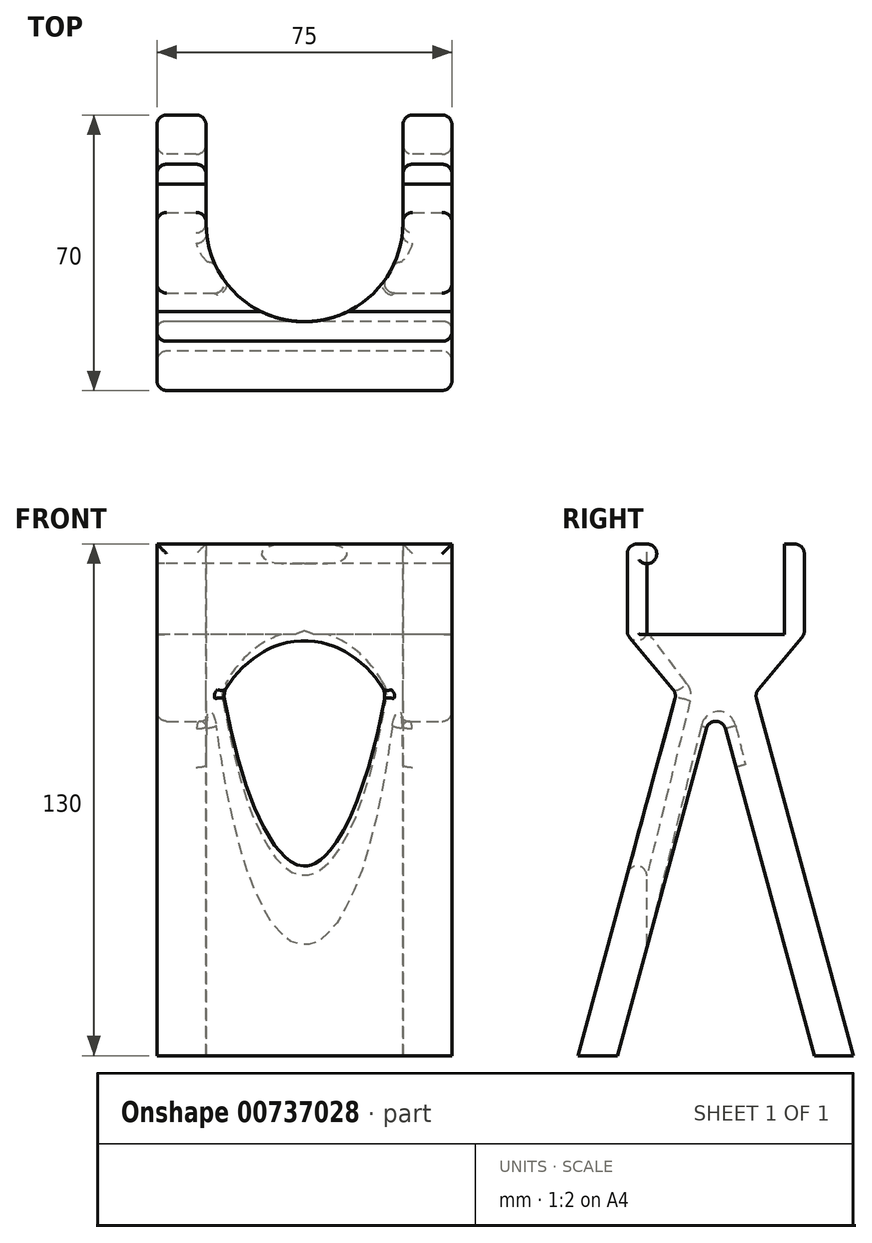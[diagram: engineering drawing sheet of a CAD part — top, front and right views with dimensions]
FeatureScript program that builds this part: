
annotation { "Feature Type Name" : "Feature", "Feature Type Description" : "" }
export const myFeature = defineFeature(function(context is Context, id is Id, definition is map)
    precondition{}
    {
        {
            var Q0;
            Q0=qCreatedBy(makeId("Right.planeOp"),FACE);
            var sketch = newSketch(context, id + "F0", { "sketchPlane" : qUnion([Q0])});
            skLineSegment(sketch, "E0", {"start": v(-104.17, 14.75) * mm, "end": v(-104.17, -8.25) * mm});
            skLineSegment(sketch, "E1", {"start": v(-104.17, -8.25) * mm, "end": v(-91.67, -23.25) * mm});
            skLineSegment(sketch, "E2", {"start": v(-91.67, -23.25) * mm, "end": v(-116.67, -115.25) * mm});
            skLineSegment(sketch, "E3", {"start": v(-116.67, -115.25) * mm, "end": v(-106.67, -115.25) * mm});
            skLineSegment(sketch, "E4", {"start": v(-106.67, -115.25) * mm, "end": v(-81.67, -23.25) * mm});
            skLineSegment(sketch, "E5", {"start": v(-81.67, -23.25) * mm, "end": v(-56.67, -115.25) * mm});
            skLineSegment(sketch, "E6", {"start": v(-56.67, -115.25) * mm, "end": v(-46.67, -115.25) * mm});
            skLineSegment(sketch, "E7", {"start": v(-46.67, -115.25) * mm, "end": v(-71.67, -23.25) * mm});
            skLineSegment(sketch, "E8", {"start": v(-71.67, -23.25) * mm, "end": v(-59.17, -8.25) * mm});
            skLineSegment(sketch, "E9", {"start": v(-59.17, -8.25) * mm, "end": v(-59.17, 14.75) * mm});
            skLineSegment(sketch, "E10", {"start": v(-59.17, 14.75) * mm, "end": v(-64.17, 14.75) * mm});
            skLineSegment(sketch, "E11", {"start": v(-64.17, 14.75) * mm, "end": v(-64.17, -8.25) * mm});
            skLineSegment(sketch, "E12", {"start": v(-64.17, -8.25) * mm, "end": v(-99.17, -8.25) * mm});
            skLineSegment(sketch, "E13", {"start": v(-99.17, -8.25) * mm, "end": v(-99.17, 9.75) * mm});
            skLineSegment(sketch, "E14", {"start": v(-99.17, 14.75) * mm, "end": v(-104.17, 14.75) * mm});
            skLineSegment(sketch, "E15", {"start": v(-81.67, -8.25) * mm, "end": v(-81.67, -125.81) * mm, "construction": true});
            skLineSegment(sketch, "E16", {"start": v(-81.67, -8.25) * mm, "end": v(-81.67, 62.4) * mm, "construction": true});
            skArc(sketch, "E17", {"start": v(-99.17, 9.75) * mm, "mid": v(-96.67, 12.25) * mm, "end": v(-99.17, 14.75) * mm});
            skSolve(sketch);
        }
        {
            var Q0;
            Q0 = qSketchRegion(id + "F0", true);
            extrude(context, id + "F1", {"entities" : qUnion([Q0]), "depth" : 75 * mm, "offsetDistance" : 25 * mm});
        }
        {
            var Q0;
            Q0=makeQuery(id+"F1.opExtrude","SWEPT_FACE",FACE,{"disambiguationData":[OSD([sQuery(id+"F0.wireOp",EDGE,"E10")])]});
            var sketch = newSketch(context, id + "F2", { "sketchPlane" : qUnion([Q0])});
            skLineSegment(sketch, "E18.bottom", {"start": v(12.5, -31.92) * mm, "end": v(62.5, -31.92) * mm});
            skLineSegment(sketch, "E18.left", {"start": v(12.5, -31.92) * mm, "end": v(12.5, -74.17) * mm});
            skLineSegment(sketch, "E18.right", {"start": v(62.5, -31.92) * mm, "end": v(62.5, -74.17) * mm});
            skArc(sketch, "E19", {"start": v(12.5, -74.17) * mm, "mid": v(37.5, -99.17) * mm, "end": v(62.5, -74.17) * mm});
            skLineSegment(sketch, "E20", {"start": v(37.5, -24.96) * mm, "end": v(37.5, -154.67) * mm, "construction": true});
            skLineSegment(sketch, "E21", {"start": v(0, -81.67) * mm, "end": v(75, -81.67) * mm, "construction": true});
            skPoint(sketch, "E22", {"position": v(37.5, -31.92) * mm});
            skPoint(sketch, "E23", {"position": v(37.5, -81.67) * mm});
            skSolve(sketch);
        }
        {
            var Q0;
            Q0 = qSketchRegion(id + "F2", true);
            var Q1;
            Q1=makeQuery(id+"F1.opExtrude","SWEPT_FACE",FACE,{"disambiguationData":[OSD([sQuery(id+"F0.wireOp",EDGE,"E6")])]});
            var Q2;
            Q2=makeQuery(id+"F1.opExtrude","SWEPT_FACE",FACE,{"disambiguationData":[OSD([sQuery(id+"F0.wireOp",EDGE,"E6")])]});
            extrude(context, id + "F3", {"entities" : qUnion([Q0]), "operationType" : NewBodyOperationType.REMOVE, "endBound" : BoundingType.UP_TO_SURFACE, "oppositeDirection" : true, "depth" : 0 * mm, "endBoundEntityFace" : qUnion([Q1]), "offsetDistance" : 25 * mm});
        }
        {
            var Q0;
            Q0=makeQuery(id+"F1.opExtrude","CAP_EDGE",EDGE,{"disambiguationData":[OSD([sQuery(id+"F0.wireOp",EDGE,"E7")])],"isStart":true});
            var Q1;
            Q1=makeQuery(id+"F1.opExtrude","CAP_EDGE",EDGE,{"disambiguationData":[OSD([sQuery(id+"F0.wireOp",EDGE,"E8")])],"isStart":true});
            var Q2;
            Q2=makeQuery(id+"F1.opExtrude","CAP_EDGE",EDGE,{"disambiguationData":[OSD([sQuery(id+"F0.wireOp",EDGE,"E9")])],"isStart":true});
            var Q3;
            {var subQ0=sQuery(id+"F0.wireOp",EDGE,"E10");var subQ1=sQuery(id+"F0.wireOp",EDGE,"E9");Q3=makeQuery(id+"F3.boolean.opBoolean","SPLIT",EDGE,{"disambiguationData":[TD([makeQuery(id+"F3.opExtrude","SWEPT_FACE",FACE,{"disambiguationData":[OSD([sQuery(id+"F2.wireOp",EDGE,"E18.left")])]})])],"derivedFrom":makeQuery(id+"F1.opExtrude","SWEPT_EDGE",EDGE,{"disambiguationData":[OSD([subQ1,subQ0])]})});}
            var Q4;
            Q4=makeQuery(id+"F3.boolean.opBoolean","INTERSECT",EDGE,{"derivedFrom":[makeQuery(id+"F1.opExtrude","SWEPT_FACE",FACE,{"disambiguationData":[OSD([sQuery(id+"F0.wireOp",EDGE,"E9")])]}),makeQuery(id+"F3.opExtrude","SWEPT_FACE",FACE,{"disambiguationData":[OSD([sQuery(id+"F2.wireOp",EDGE,"E18.left")])]})]});
            var Q5;
            Q5=makeQuery(id+"F3.boolean.opBoolean","INTERSECT",EDGE,{"derivedFrom":[makeQuery(id+"F1.opExtrude","SWEPT_FACE",FACE,{"disambiguationData":[OSD([sQuery(id+"F0.wireOp",EDGE,"E8")])]}),makeQuery(id+"F3.opExtrude","SWEPT_FACE",FACE,{"disambiguationData":[OSD([sQuery(id+"F2.wireOp",EDGE,"E18.left")])]})]});
            var Q6;
            Q6=makeQuery(id+"F3.boolean.opBoolean","INTERSECT",EDGE,{"derivedFrom":[makeQuery(id+"F1.opExtrude","SWEPT_FACE",FACE,{"disambiguationData":[OSD([sQuery(id+"F0.wireOp",EDGE,"E7")])]}),makeQuery(id+"F3.opExtrude","SWEPT_FACE",FACE,{"disambiguationData":[OSD([sQuery(id+"F2.wireOp",EDGE,"E18.left")])]})]});
            var Q7;
            {var subQ0=sQuery(id+"F0.wireOp",EDGE,"E8");var subQ1=sQuery(id+"F0.wireOp",EDGE,"E7");Q7=makeQuery(id+"F3.boolean.opBoolean","SPLIT",EDGE,{"disambiguationData":[TD([makeQuery(id+"F3.opExtrude","SWEPT_FACE",FACE,{"disambiguationData":[OSD([sQuery(id+"F2.wireOp",EDGE,"E18.left")])]})])],"derivedFrom":makeQuery(id+"F1.opExtrude","SWEPT_EDGE",EDGE,{"disambiguationData":[OSD([subQ1,subQ0])]})});}
            var Q8;
            {var subQ0=sQuery(id+"F0.wireOp",EDGE,"E9");var subQ1=sQuery(id+"F0.wireOp",EDGE,"E8");Q8=makeQuery(id+"F3.boolean.opBoolean","SPLIT",EDGE,{"disambiguationData":[TD([makeQuery(id+"F3.opExtrude","SWEPT_FACE",FACE,{"disambiguationData":[OSD([sQuery(id+"F2.wireOp",EDGE,"E18.left")])]})])],"derivedFrom":makeQuery(id+"F1.opExtrude","SWEPT_EDGE",EDGE,{"disambiguationData":[OSD([subQ1,subQ0])]})});}
            var Q9;
            Q9=makeQuery(id+"F3.boolean.opBoolean","INTERSECT",EDGE,{"derivedFrom":[makeQuery(id+"F1.opExtrude","SWEPT_FACE",FACE,{"disambiguationData":[OSD([sQuery(id+"F0.wireOp",EDGE,"E7")])]}),makeQuery(id+"F3.opExtrude","SWEPT_FACE",FACE,{"disambiguationData":[OSD([sQuery(id+"F2.wireOp",EDGE,"E18.right")])]})]});
            var Q10;
            Q10=makeQuery(id+"F3.boolean.opBoolean","INTERSECT",EDGE,{"derivedFrom":[makeQuery(id+"F1.opExtrude","SWEPT_FACE",FACE,{"disambiguationData":[OSD([sQuery(id+"F0.wireOp",EDGE,"E8")])]}),makeQuery(id+"F3.opExtrude","SWEPT_FACE",FACE,{"disambiguationData":[OSD([sQuery(id+"F2.wireOp",EDGE,"E18.right")])]})]});
            var Q11;
            Q11=makeQuery(id+"F3.boolean.opBoolean","INTERSECT",EDGE,{"derivedFrom":[makeQuery(id+"F1.opExtrude","SWEPT_FACE",FACE,{"disambiguationData":[OSD([sQuery(id+"F0.wireOp",EDGE,"E9")])]}),makeQuery(id+"F3.opExtrude","SWEPT_FACE",FACE,{"disambiguationData":[OSD([sQuery(id+"F2.wireOp",EDGE,"E18.right")])]})]});
            var Q12;
            {var subQ0=sQuery(id+"F0.wireOp",EDGE,"E10");var subQ1=sQuery(id+"F0.wireOp",EDGE,"E9");Q12=makeQuery(id+"F3.boolean.opBoolean","SPLIT",EDGE,{"disambiguationData":[TD([makeQuery(id+"F3.opExtrude","SWEPT_FACE",FACE,{"disambiguationData":[OSD([sQuery(id+"F2.wireOp",EDGE,"E18.right")])]})])],"derivedFrom":makeQuery(id+"F1.opExtrude","SWEPT_EDGE",EDGE,{"disambiguationData":[OSD([subQ1,subQ0])]})});}
            var Q13;
            Q13=makeQuery(id+"F1.opExtrude","CAP_EDGE",EDGE,{"disambiguationData":[OSD([sQuery(id+"F0.wireOp",EDGE,"E9")])],"isStart":false});
            var Q14;
            Q14=makeQuery(id+"F1.opExtrude","CAP_EDGE",EDGE,{"disambiguationData":[OSD([sQuery(id+"F0.wireOp",EDGE,"E8")])],"isStart":false});
            var Q15;
            Q15=makeQuery(id+"F1.opExtrude","CAP_EDGE",EDGE,{"disambiguationData":[OSD([sQuery(id+"F0.wireOp",EDGE,"E7")])],"isStart":false});
            var Q16;
            {var subQ0=sQuery(id+"F0.wireOp",EDGE,"E8");var subQ1=sQuery(id+"F0.wireOp",EDGE,"E7");Q16=makeQuery(id+"F3.boolean.opBoolean","SPLIT",EDGE,{"disambiguationData":[TD([makeQuery(id+"F3.opExtrude","SWEPT_FACE",FACE,{"disambiguationData":[OSD([sQuery(id+"F2.wireOp",EDGE,"E18.right")])]})])],"derivedFrom":makeQuery(id+"F1.opExtrude","SWEPT_EDGE",EDGE,{"disambiguationData":[OSD([subQ1,subQ0])]})});}
            var Q17;
            {var subQ0=sQuery(id+"F0.wireOp",EDGE,"E9");var subQ1=sQuery(id+"F0.wireOp",EDGE,"E8");Q17=makeQuery(id+"F3.boolean.opBoolean","SPLIT",EDGE,{"disambiguationData":[TD([makeQuery(id+"F3.opExtrude","SWEPT_FACE",FACE,{"disambiguationData":[OSD([sQuery(id+"F2.wireOp",EDGE,"E18.right")])]})])],"derivedFrom":makeQuery(id+"F1.opExtrude","SWEPT_EDGE",EDGE,{"disambiguationData":[OSD([subQ1,subQ0])]})});}
            var Q18;
            Q18=makeQuery(id+"F1.opExtrude","CAP_EDGE",EDGE,{"disambiguationData":[OSD([sQuery(id+"F0.wireOp",EDGE,"E5")])],"isStart":false});
            var Q19;
            Q19=makeQuery(id+"F3.boolean.opBoolean","INTERSECT",EDGE,{"derivedFrom":[makeQuery(id+"F1.opExtrude","SWEPT_FACE",FACE,{"disambiguationData":[OSD([sQuery(id+"F0.wireOp",EDGE,"E5")])]}),makeQuery(id+"F3.opExtrude","SWEPT_FACE",FACE,{"disambiguationData":[OSD([sQuery(id+"F2.wireOp",EDGE,"E18.right")])]})]});
            var Q20;
            Q20=makeQuery(id+"F1.opExtrude","CAP_EDGE",EDGE,{"disambiguationData":[OSD([sQuery(id+"F0.wireOp",EDGE,"E4")])],"isStart":false});
            var Q21;
            Q21=makeQuery(id+"F1.opExtrude","CAP_EDGE",EDGE,{"disambiguationData":[OSD([sQuery(id+"F0.wireOp",EDGE,"E4")])],"isStart":true});
            var Q22;
            Q22=makeQuery(id+"F3.boolean.opBoolean","INTERSECT",EDGE,{"derivedFrom":[makeQuery(id+"F1.opExtrude","SWEPT_FACE",FACE,{"disambiguationData":[OSD([sQuery(id+"F0.wireOp",EDGE,"E4")])]}),makeQuery(id+"F3.opExtrude","SWEPT_FACE",FACE,{"disambiguationData":[OSD([sQuery(id+"F2.wireOp",EDGE,"E19")])]})]});
            var Q23;
            Q23=makeQuery(id+"F3.boolean.opBoolean","INTERSECT",EDGE,{"derivedFrom":[makeQuery(id+"F1.opExtrude","SWEPT_FACE",FACE,{"disambiguationData":[OSD([sQuery(id+"F0.wireOp",EDGE,"E2")])]}),makeQuery(id+"F3.opExtrude","SWEPT_FACE",FACE,{"disambiguationData":[OSD([sQuery(id+"F2.wireOp",EDGE,"E19")])]})]});
            var Q24;
            Q24=makeQuery(id+"F3.boolean.opBoolean","INTERSECT",EDGE,{"derivedFrom":[makeQuery(id+"F1.opExtrude","SWEPT_FACE",FACE,{"disambiguationData":[OSD([sQuery(id+"F0.wireOp",EDGE,"E1")])]}),makeQuery(id+"F3.opExtrude","SWEPT_FACE",FACE,{"disambiguationData":[OSD([sQuery(id+"F2.wireOp",EDGE,"E19")])]})]});
            var Q25;
            Q25=makeQuery(id+"F1.opExtrude","CAP_EDGE",EDGE,{"disambiguationData":[OSD([sQuery(id+"F0.wireOp",EDGE,"E2")])],"isStart":false});
            var Q26;
            Q26=makeQuery(id+"F1.opExtrude","CAP_EDGE",EDGE,{"disambiguationData":[OSD([sQuery(id+"F0.wireOp",EDGE,"E2")])],"isStart":true});
            var Q27;
            Q27=makeQuery(id+"F1.opExtrude","CAP_EDGE",EDGE,{"disambiguationData":[OSD([sQuery(id+"F0.wireOp",EDGE,"E5")])],"isStart":true});
            var Q28;
            Q28=makeQuery(id+"F3.boolean.opBoolean","INTERSECT",EDGE,{"derivedFrom":[makeQuery(id+"F1.opExtrude","SWEPT_FACE",FACE,{"disambiguationData":[OSD([sQuery(id+"F0.wireOp",EDGE,"E5")])]}),makeQuery(id+"F3.opExtrude","SWEPT_FACE",FACE,{"disambiguationData":[OSD([sQuery(id+"F2.wireOp",EDGE,"E18.left")])]})]});
            var Q29;
            Q29=makeQuery(id+"F1.opExtrude","SWEPT_EDGE",EDGE,{"disambiguationData":[OSD([sQuery(id+"F0.wireOp",EDGE,"E0"),sQuery(id+"F0.wireOp",EDGE,"E14")])]});
            var Q30;
            Q30=makeQuery(id+"F1.opExtrude","CAP_EDGE",EDGE,{"disambiguationData":[OSD([sQuery(id+"F0.wireOp",EDGE,"E1")])],"isStart":true});
            var Q31;
            Q31=makeQuery(id+"F1.opExtrude","CAP_EDGE",EDGE,{"disambiguationData":[OSD([sQuery(id+"F0.wireOp",EDGE,"E0")])],"isStart":true});
            var Q32;
            Q32=makeQuery(id+"F1.opExtrude","CAP_EDGE",EDGE,{"disambiguationData":[OSD([sQuery(id+"F0.wireOp",EDGE,"E1")])],"isStart":false});
            var Q33;
            Q33=makeQuery(id+"F1.opExtrude","CAP_EDGE",EDGE,{"disambiguationData":[OSD([sQuery(id+"F0.wireOp",EDGE,"E0")])],"isStart":false});
            var Q34;
            {var subQ0=sQuery(id+"F0.wireOp",EDGE,"E2");var subQ1=sQuery(id+"F0.wireOp",EDGE,"E1");Q34=makeQuery(id+"F3.boolean.opBoolean","SPLIT",EDGE,{"disambiguationData":[TD([makeQuery(id+"F1.opExtrude","CAP_FACE",FACE,{"disambiguationData":[OSD([sQuery(id+"F0.wireOp",EDGE,"E0"),subQ1,subQ0,sQuery(id+"F0.wireOp",EDGE,"E3"),sQuery(id+"F0.wireOp",EDGE,"E4"),sQuery(id+"F0.wireOp",EDGE,"E5"),sQuery(id+"F0.wireOp",EDGE,"E6"),sQuery(id+"F0.wireOp",EDGE,"E7"),sQuery(id+"F0.wireOp",EDGE,"E8"),sQuery(id+"F0.wireOp",EDGE,"E9"),sQuery(id+"F0.wireOp",EDGE,"E10"),sQuery(id+"F0.wireOp",EDGE,"E11"),sQuery(id+"F0.wireOp",EDGE,"E12"),sQuery(id+"F0.wireOp",EDGE,"E13"),sQuery(id+"F0.wireOp",EDGE,"E14"),sQuery(id+"F0.wireOp",EDGE,"E17")])],"isStart":true})])],"derivedFrom":makeQuery(id+"F1.opExtrude","SWEPT_EDGE",EDGE,{"disambiguationData":[OSD([subQ1,subQ0])]})});}
            var Q35;
            {var subQ0=sQuery(id+"F0.wireOp",EDGE,"E2");var subQ1=sQuery(id+"F0.wireOp",EDGE,"E1");Q35=makeQuery(id+"F3.boolean.opBoolean","SPLIT",EDGE,{"disambiguationData":[TD([makeQuery(id+"F1.opExtrude","CAP_FACE",FACE,{"disambiguationData":[OSD([sQuery(id+"F0.wireOp",EDGE,"E0"),subQ1,subQ0,sQuery(id+"F0.wireOp",EDGE,"E3"),sQuery(id+"F0.wireOp",EDGE,"E4"),sQuery(id+"F0.wireOp",EDGE,"E5"),sQuery(id+"F0.wireOp",EDGE,"E6"),sQuery(id+"F0.wireOp",EDGE,"E7"),sQuery(id+"F0.wireOp",EDGE,"E8"),sQuery(id+"F0.wireOp",EDGE,"E9"),sQuery(id+"F0.wireOp",EDGE,"E10"),sQuery(id+"F0.wireOp",EDGE,"E11"),sQuery(id+"F0.wireOp",EDGE,"E12"),sQuery(id+"F0.wireOp",EDGE,"E13"),sQuery(id+"F0.wireOp",EDGE,"E14"),sQuery(id+"F0.wireOp",EDGE,"E17")])],"isStart":false})])],"derivedFrom":makeQuery(id+"F1.opExtrude","SWEPT_EDGE",EDGE,{"disambiguationData":[OSD([subQ1,subQ0])]})});}
            var Q36;
            {var subQ0=sQuery(id+"F0.wireOp",EDGE,"E5");var subQ1=sQuery(id+"F0.wireOp",EDGE,"E4");Q36=makeQuery(id+"F3.boolean.opBoolean","SPLIT",EDGE,{"disambiguationData":[TD([makeQuery(id+"F1.opExtrude","CAP_FACE",FACE,{"disambiguationData":[OSD([sQuery(id+"F0.wireOp",EDGE,"E0"),sQuery(id+"F0.wireOp",EDGE,"E1"),sQuery(id+"F0.wireOp",EDGE,"E2"),sQuery(id+"F0.wireOp",EDGE,"E3"),subQ1,subQ0,sQuery(id+"F0.wireOp",EDGE,"E6"),sQuery(id+"F0.wireOp",EDGE,"E7"),sQuery(id+"F0.wireOp",EDGE,"E8"),sQuery(id+"F0.wireOp",EDGE,"E9"),sQuery(id+"F0.wireOp",EDGE,"E10"),sQuery(id+"F0.wireOp",EDGE,"E11"),sQuery(id+"F0.wireOp",EDGE,"E12"),sQuery(id+"F0.wireOp",EDGE,"E13"),sQuery(id+"F0.wireOp",EDGE,"E14"),sQuery(id+"F0.wireOp",EDGE,"E17")])],"isStart":false})])],"derivedFrom":makeQuery(id+"F1.opExtrude","SWEPT_EDGE",EDGE,{"disambiguationData":[OSD([subQ1,subQ0])]})});}
            var Q37;
            {var subQ0=sQuery(id+"F0.wireOp",EDGE,"E5");var subQ1=sQuery(id+"F0.wireOp",EDGE,"E4");Q37=makeQuery(id+"F3.boolean.opBoolean","SPLIT",EDGE,{"disambiguationData":[TD([makeQuery(id+"F1.opExtrude","CAP_FACE",FACE,{"disambiguationData":[OSD([sQuery(id+"F0.wireOp",EDGE,"E0"),sQuery(id+"F0.wireOp",EDGE,"E1"),sQuery(id+"F0.wireOp",EDGE,"E2"),sQuery(id+"F0.wireOp",EDGE,"E3"),subQ1,subQ0,sQuery(id+"F0.wireOp",EDGE,"E6"),sQuery(id+"F0.wireOp",EDGE,"E7"),sQuery(id+"F0.wireOp",EDGE,"E8"),sQuery(id+"F0.wireOp",EDGE,"E9"),sQuery(id+"F0.wireOp",EDGE,"E10"),sQuery(id+"F0.wireOp",EDGE,"E11"),sQuery(id+"F0.wireOp",EDGE,"E12"),sQuery(id+"F0.wireOp",EDGE,"E13"),sQuery(id+"F0.wireOp",EDGE,"E14"),sQuery(id+"F0.wireOp",EDGE,"E17")])],"isStart":true})])],"derivedFrom":makeQuery(id+"F1.opExtrude","SWEPT_EDGE",EDGE,{"disambiguationData":[OSD([subQ1,subQ0])]})});}
            var Q38;
            Q38=makeQuery(id+"F1.opExtrude","SWEPT_EDGE",EDGE,{"disambiguationData":[OSD([sQuery(id+"F0.wireOp",EDGE,"E0"),sQuery(id+"F0.wireOp",EDGE,"E1")])]});
            fillet(context, id + "F4", {"entities" : qUnion([Q0, Q1, Q2, Q3, Q4, Q5, Q6, Q7, Q8, Q9, Q10, Q11, Q12, Q13, Q14, Q15, Q16, Q17, Q18, Q19, Q20, Q21, Q22, Q23, Q24, Q25, Q26, Q27, Q28, Q29, Q30, Q31, Q32, Q33, Q34, Q35, Q36, Q37, Q38]), "radius" : 2.5 * mm, "tangentPropagation" : true, "allowEdgeOverflow" : false});
        }
        {
            var Q0;
            Q0=makeQuery(id+"F3.boolean.opBoolean","INTERSECT",EDGE,{"derivedFrom":[makeQuery(id+"F1.opExtrude","SWEPT_FACE",FACE,{"disambiguationData":[OSD([sQuery(id+"F0.wireOp",EDGE,"E2")])]}),makeQuery(id+"F3.opExtrude","SWEPT_FACE",FACE,{"disambiguationData":[OSD([sQuery(id+"F2.wireOp",EDGE,"E19")])]})]});
            var Q1;
            Q1=makeQuery(id+"F3.boolean.opBoolean","INTERSECT",EDGE,{"derivedFrom":[makeQuery(id+"F1.opExtrude","SWEPT_FACE",FACE,{"disambiguationData":[OSD([sQuery(id+"F0.wireOp",EDGE,"E4")])]}),makeQuery(id+"F3.opExtrude","SWEPT_FACE",FACE,{"disambiguationData":[OSD([sQuery(id+"F2.wireOp",EDGE,"E19")])]})]});
            var Q2;
            Q2=makeQuery(id+"F1.opExtrude","CAP_EDGE",EDGE,{"disambiguationData":[OSD([sQuery(id+"F0.wireOp",EDGE,"E13")])],"isStart":false});
            var Q3;
            Q3=makeQuery(id+"F1.opExtrude","CAP_EDGE",EDGE,{"disambiguationData":[OSD([sQuery(id+"F0.wireOp",EDGE,"E13")])],"isStart":true});
            fillet(context, id + "F5", {"entities" : qUnion([Q0, Q1, Q2, Q3]), "radius" : 2 * mm, "tangentPropagation" : true, "allowEdgeOverflow" : false});
        }
    });
